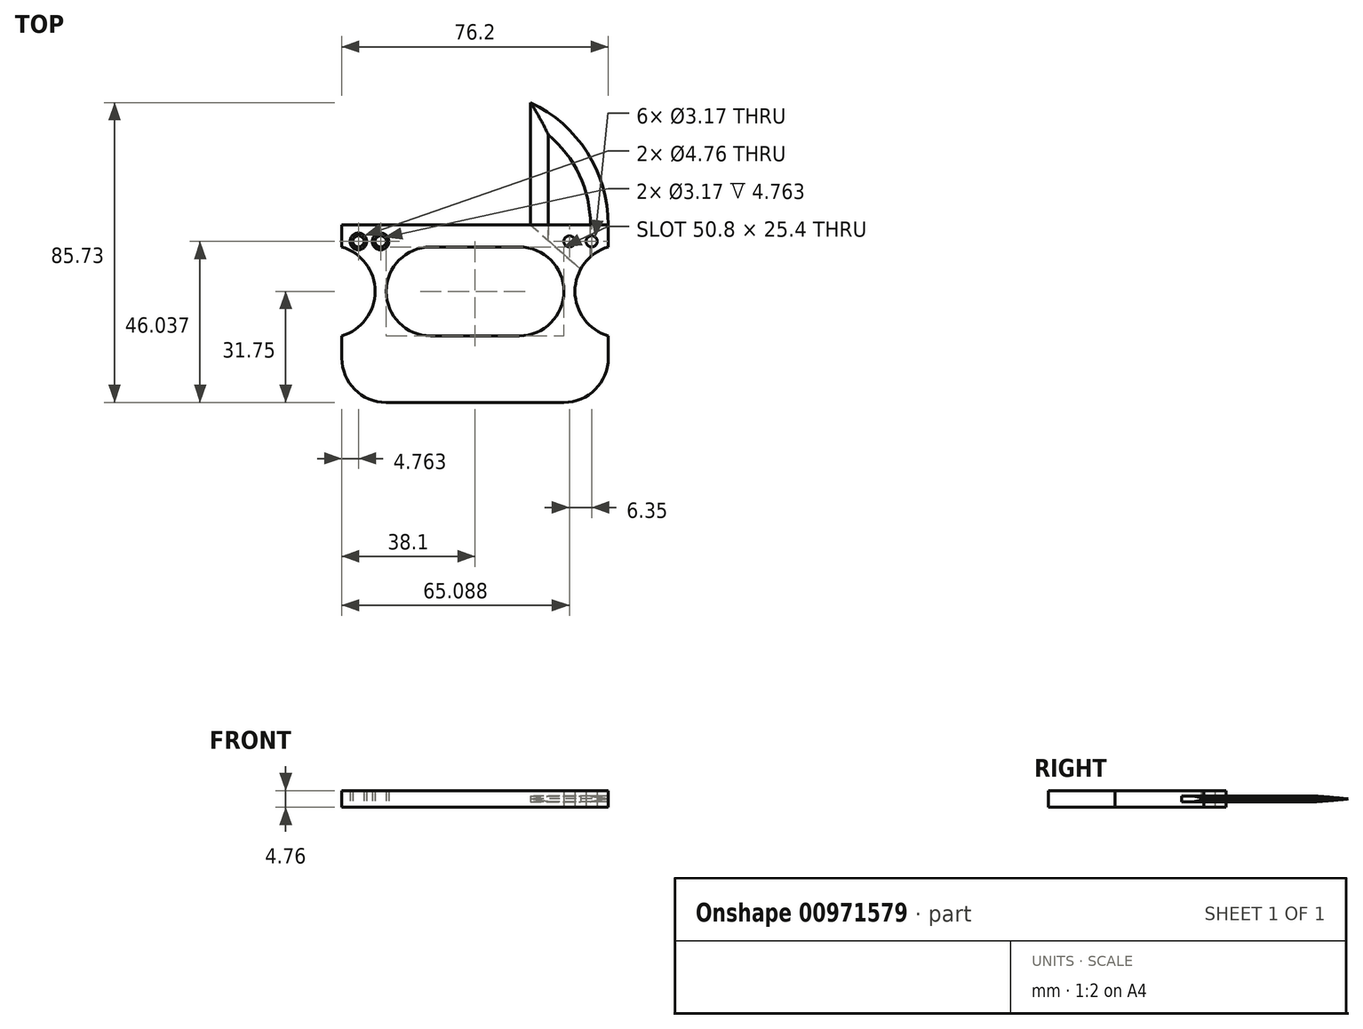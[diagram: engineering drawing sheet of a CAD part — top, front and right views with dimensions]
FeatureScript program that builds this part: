
annotation { "Feature Type Name" : "Feature", "Feature Type Description" : "" }
export const myFeature = defineFeature(function(context is Context, id is Id, definition is map)
    precondition{}
    {
        {
            var Q0;
            Q0=qCreatedBy(makeId("Top.planeOp"),FACE);
            var sketch = newSketch(context, id + "F0", { "sketchPlane" : qUnion([Q0])});
            skLineSegment(sketch, "E0.bottom", {"start": v(25.4, -25.4) * mm, "end": v(-25.4, -25.4) * mm});
            skLineSegment(sketch, "E0.top", {"start": v(38.1, 25.4) * mm, "end": v(-38.1, 25.4) * mm});
            skLineSegment(sketch, "E0.left", {"start": v(38.1, -12.7) * mm, "end": v(38.1, -6.35) * mm});
            skLineSegment(sketch, "E0.right", {"start": v(-38.1, -12.7) * mm, "end": v(-38.1, -6.35) * mm});
            skPoint(sketch, "E0.middle", {"position": v(0, 0) * mm});
            skArc(sketch, "E1", {"start": v(-12.7, -6.35) * mm, "mid": v(-25.4, 6.35) * mm, "end": v(-12.7, 19.05) * mm});
            skArc(sketch, "E2", {"start": v(12.7, -6.35) * mm, "mid": v(25.4, 6.35) * mm, "end": v(12.7, 19.05) * mm});
            skLineSegment(sketch, "E3", {"start": v(-12.7, 19.05) * mm, "end": v(12.7, 19.05) * mm});
            skLineSegment(sketch, "E4", {"start": v(12.7, -6.35) * mm, "end": v(-12.7, -6.35) * mm});
            skArc(sketch, "E5", {"start": v(38.1, 19.05) * mm, "mid": v(28.57, 6.35) * mm, "end": v(38.1, -6.35) * mm});
            skArc(sketch, "E6", {"start": v(-38.1, -6.35) * mm, "mid": v(-28.58, 6.35) * mm, "end": v(-38.1, 19.05) * mm});
            skPoint(sketch, "E7.visualSharp", {"position": v(-38.1, -25.4) * mm});
            skArc(sketch, "E7.filletArc", {"start": v(-38.1, -12.7) * mm, "mid": v(-34.38, -21.68) * mm, "end": v(-25.4, -25.4) * mm});
            skPoint(sketch, "E8.visualSharp", {"position": v(38.1, -25.4) * mm});
            skArc(sketch, "E8.filletArc", {"start": v(25.4, -25.4) * mm, "mid": v(34.38, -21.68) * mm, "end": v(38.1, -12.7) * mm});
            skLineSegment(sketch, "E9.trimOffspring", {"start": v(38.1, 19.05) * mm, "end": v(38.1, 25.4) * mm});
            skLineSegment(sketch, "E10.trimOffspring", {"start": v(-38.1, 19.05) * mm, "end": v(-38.1, 25.4) * mm});
            skSolve(sketch);
        }
        {
            var Q0;
            Q0=makeQuery(id+"F0.imprint","IMPRINT",FACE,{"disambiguationData":[TD([[makeQuery(id+"F0.imprint","IMPRINT",EDGE,{"derivedFrom":sQuery(id+"F0.wireOp",EDGE,"E0.bottom")}),-1.0]])]});
            extrude(context, id + "F1", {"entities" : qUnion([Q0]), "depth" : 2.38 * mm, "offsetDistance" : 25.4 * mm, "hasSecondDirection" : true, "secondDirectionOppositeDirection" : true, "secondDirectionDepth" : 2.38 * mm});
        }
        {
            var Q0;
            Q0=qCreatedBy(makeId("Top.planeOp"),FACE);
            var sketch = newSketch(context, id + "F2", { "sketchPlane" : qUnion([Q0])});
            skLineSegment(sketch, "E11", {"start": v(15.87, 25.4) * mm, "end": v(30.2, 12.7) * mm});
            skArc(sketch, "E12", {"start": v(38.1, -6.35) * mm, "mid": v(28.58, 6.35) * mm, "end": v(38.1, 19.05) * mm});
            skLineSegment(sketch, "E13", {"start": v(38.1, 19.05) * mm, "end": v(38.1, 25.4) * mm});
            skLineSegment(sketch, "E14", {"start": v(15.87, 25.4) * mm, "end": v(15.87, 60.33) * mm});
            skArc(sketch, "E15", {"start": v(38.1, 25.4) * mm, "mid": v(32.07, 46.1) * mm, "end": v(15.87, 60.33) * mm});
            skLineSegment(sketch, "E16", {"start": v(0, 60.33) * mm, "end": v(0, -6.35) * mm, "construction": true});
            skArc(sketch, "E17.MirrorCS", {"start": v(-38.1, 25.4) * mm, "mid": v(-32.07, 46.1) * mm, "end": v(-15.87, 60.33) * mm});
            skLineSegment(sketch, "E18.MirrorCS", {"start": v(-15.87, 25.4) * mm, "end": v(-15.87, 60.33) * mm});
            skLineSegment(sketch, "E19.MirrorCS", {"start": v(-15.87, 25.4) * mm, "end": v(-30.2, 12.7) * mm});
            skArc(sketch, "E20.MirrorCS", {"start": v(-38.1, -6.35) * mm, "mid": v(-28.58, 6.35) * mm, "end": v(-38.1, 19.05) * mm});
            skLineSegment(sketch, "E21.MirrorCS", {"start": v(-38.1, 19.05) * mm, "end": v(-38.1, 25.4) * mm});
            skSolve(sketch);
        }
        {
            var Q0;
            Q0=makeQuery(id+"F2.imprint","IMPRINT",FACE,{"disambiguationData":[TD([[makeQuery(id+"F2.imprint","IMPRINT",EDGE,{"derivedFrom":sQuery(id+"F2.wireOp",EDGE,"E17.MirrorCS")}),-1.0]])]});
            var Q1;
            {var subQ2=sQuery(id+"F2.wireOp",EDGE,"E11");Q1=makeQuery(id+"F2.imprint","IMPRINT",FACE,{"disambiguationData":[TD([[makeQuery(id+"F2.imprint","IMPRINT",EDGE,{"derivedFrom":subQ2}),1.0]])]});}
            extrude(context, id + "F3", {"entities" : qUnion([Q0, Q1]), "operationType" : NewBodyOperationType.REMOVE, "depth" : 0.8 * mm, "offsetDistance" : 25.4 * mm, "hasSecondDirection" : true, "secondDirectionOppositeDirection" : true, "secondDirectionDepth" : 0.8 * mm});
        }
        {
            var Q0;
            {var subQ2=sQuery(id+"F2.wireOp",EDGE,"E11");Q0=makeQuery(id+"F2.imprint","IMPRINT",FACE,{"disambiguationData":[TD([[makeQuery(id+"F2.imprint","IMPRINT",EDGE,{"derivedFrom":subQ2}),1.0]])]});}
            var Q1;
            Q1=makeQuery(id+"F2.imprint","IMPRINT",FACE,{"disambiguationData":[TD([[makeQuery(id+"F2.imprint","IMPRINT",EDGE,{"derivedFrom":sQuery(id+"F2.wireOp",EDGE,"E17.MirrorCS")}),-1.0]])]});
            extrude(context, id + "F4", {"entities" : qUnion([Q0, Q1]), "depth" : 0.8 * mm, "offsetDistance" : 25.4 * mm, "hasSecondDirection" : true, "secondDirectionOppositeDirection" : true, "secondDirectionDepth" : 0.8 * mm});
        }
        {
            var Q0;
            Q0=qCreatedBy(makeId("Top.planeOp"),FACE);
            var sketch = newSketch(context, id + "F5", { "sketchPlane" : qUnion([Q0])});
            skCircle(sketch, "E22", {"center": v(33.34, 20.64) * mm, "radius": 1.59 * mm});
            skCircle(sketch, "E23", {"center": v(26.99, 20.64) * mm, "radius": 1.59 * mm});
            skLineSegment(sketch, "E24", {"start": v(0, 26.48) * mm, "end": v(0, 14.72) * mm, "construction": true});
            skCircle(sketch, "E25.MirrorC", {"center": v(-26.99, 20.64) * mm, "radius": 1.59 * mm});
            skCircle(sketch, "E26.MirrorC", {"center": v(-33.34, 20.64) * mm, "radius": 1.59 * mm});
            skCircle(sketch, "E27", {"center": v(33.34, 20.64) * mm, "radius": 2.38 * mm});
            skCircle(sketch, "E28", {"center": v(26.99, 20.64) * mm, "radius": 2.38 * mm});
            skCircle(sketch, "E29.MirrorC", {"center": v(-26.99, 20.64) * mm, "radius": 2.38 * mm});
            skCircle(sketch, "E30.MirrorC", {"center": v(-33.34, 20.64) * mm, "radius": 2.38 * mm});
            skSolve(sketch);
        }
        {
            var Q0;
            Q0=makeQuery(id+"F5.imprint","IMPRINT",FACE,{"disambiguationData":[TD([[makeQuery(id+"F5.imprint","IMPRINT",EDGE,{"derivedFrom":sQuery(id+"F5.wireOp",EDGE,"E25.MirrorC")}),-1.0]])]});
            var Q1;
            Q1=makeQuery(id+"F5.imprint","IMPRINT",FACE,{"disambiguationData":[TD([[makeQuery(id+"F5.imprint","IMPRINT",EDGE,{"derivedFrom":sQuery(id+"F5.wireOp",EDGE,"E23")}),1.0]])]});
            var Q2;
            Q2=makeQuery(id+"F5.imprint","IMPRINT",FACE,{"disambiguationData":[TD([[makeQuery(id+"F5.imprint","IMPRINT",EDGE,{"derivedFrom":sQuery(id+"F5.wireOp",EDGE,"E26.MirrorC")}),-1.0]])]});
            var Q3;
            Q3=makeQuery(id+"F5.imprint","IMPRINT",FACE,{"disambiguationData":[TD([[makeQuery(id+"F5.imprint","IMPRINT",EDGE,{"derivedFrom":sQuery(id+"F5.wireOp",EDGE,"E22")}),1.0]])]});
            extrude(context, id + "F6", {"entities" : qUnion([Q0, Q1, Q2, Q3]), "operationType" : NewBodyOperationType.REMOVE, "depth" : 2.38 * mm, "offsetDistance" : 25.4 * mm, "hasSecondDirection" : true, "secondDirectionOppositeDirection" : true, "secondDirectionDepth" : 2.38 * mm});
        }
        {
            var Q0;
            Q0=makeQuery(id+"F5.imprint","IMPRINT",FACE,{"disambiguationData":[TD([[makeQuery(id+"F5.imprint","IMPRINT",EDGE,{"derivedFrom":sQuery(id+"F5.wireOp",EDGE,"E26.MirrorC")}),-1.0]])]});
            var Q1;
            Q1=makeQuery(id+"F5.imprint","IMPRINT",FACE,{"disambiguationData":[TD([[makeQuery(id+"F5.imprint","IMPRINT",EDGE,{"derivedFrom":sQuery(id+"F5.wireOp",EDGE,"E25.MirrorC")}),-1.0]])]});
            var Q2;
            Q2=makeQuery(id+"F5.imprint","IMPRINT",FACE,{"disambiguationData":[TD([[makeQuery(id+"F5.imprint","IMPRINT",EDGE,{"derivedFrom":sQuery(id+"F5.wireOp",EDGE,"E23")}),1.0]])]});
            var Q3;
            Q3=makeQuery(id+"F5.imprint","IMPRINT",FACE,{"disambiguationData":[TD([[makeQuery(id+"F5.imprint","IMPRINT",EDGE,{"derivedFrom":sQuery(id+"F5.wireOp",EDGE,"E22")}),1.0]])]});
            extrude(context, id + "F7", {"entities" : qUnion([Q0, Q1, Q2, Q3]), "depth" : 2.38 * mm, "offsetDistance" : 25.4 * mm, "hasSecondDirection" : true, "secondDirectionOppositeDirection" : true, "secondDirectionDepth" : 2.38 * mm});
        }
        {
            var Q0;
            Q0=makeQuery(id+"F4.opExtrude","CAP_EDGE",EDGE,{"disambiguationData":[OSD([sQuery(id+"F2.wireOp",EDGE,"E18.MirrorCS")])],"isStart":false});
            var Q1;
            Q1=makeQuery(id+"F4.opExtrude","CAP_EDGE",EDGE,{"disambiguationData":[OSD([sQuery(id+"F2.wireOp",EDGE,"E17.MirrorCS")])],"isStart":false});
            var Q2;
            Q2=makeQuery(id+"F4.opExtrude","CAP_EDGE",EDGE,{"disambiguationData":[OSD([sQuery(id+"F2.wireOp",EDGE,"E15")])],"isStart":false});
            var Q3;
            Q3=makeQuery(id+"F4.opExtrude","CAP_EDGE",EDGE,{"disambiguationData":[OSD([sQuery(id+"F2.wireOp",EDGE,"E14")])],"isStart":false});
            chamfer(context, id + "F8", {"entities" : qUnion([Q0, Q1, Q2, Q3]), "chamferType" : ChamferType.TWO_OFFSETS, "width1" : 0.8 * mm, "oppositeDirection" : true, "width2" : 5.08 * mm, "tangentPropagation" : true});
        }
        {
            var Q0;
            Q0=makeQuery(id+"F4.opExtrude","CAP_EDGE",EDGE,{"disambiguationData":[OSD([sQuery(id+"F2.wireOp",EDGE,"E15")])],"isStart":true});
            var Q1;
            Q1=makeQuery(id+"F4.opExtrude","CAP_EDGE",EDGE,{"disambiguationData":[OSD([sQuery(id+"F2.wireOp",EDGE,"E14")])],"isStart":true});
            var Q2;
            Q2=makeQuery(id+"F4.opExtrude","CAP_EDGE",EDGE,{"disambiguationData":[OSD([sQuery(id+"F2.wireOp",EDGE,"E18.MirrorCS")])],"isStart":true});
            var Q3;
            Q3=makeQuery(id+"F4.opExtrude","CAP_EDGE",EDGE,{"disambiguationData":[OSD([sQuery(id+"F2.wireOp",EDGE,"E17.MirrorCS")])],"isStart":true});
            chamfer(context, id + "F9", {"entities" : qUnion([Q0, Q1, Q2, Q3]), "chamferType" : ChamferType.TWO_OFFSETS, "width1" : 0.8 * mm, "oppositeDirection" : false, "width2" : 5.08 * mm, "tangentPropagation" : true});
        }
    });
